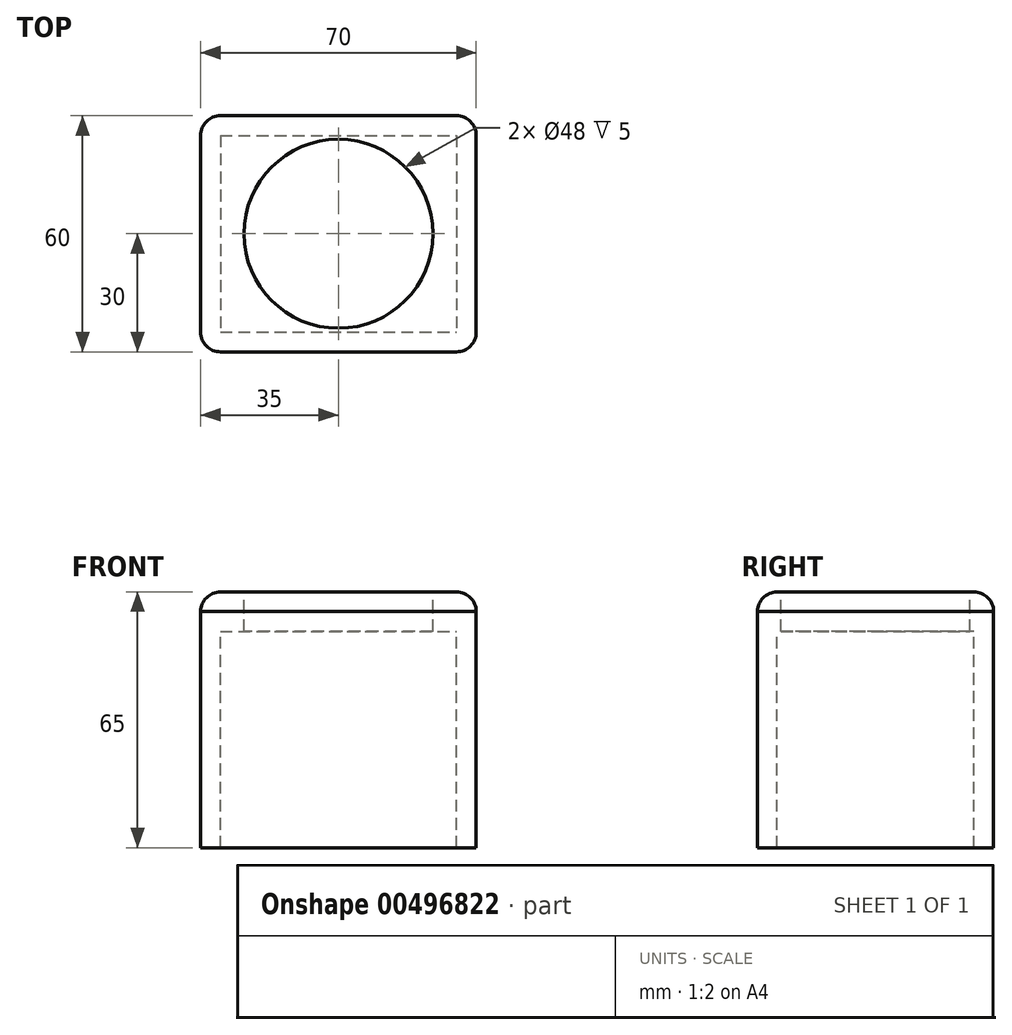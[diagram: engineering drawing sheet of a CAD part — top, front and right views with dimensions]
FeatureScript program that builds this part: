
annotation { "Feature Type Name" : "Feature", "Feature Type Description" : "" }
export const myFeature = defineFeature(function(context is Context, id is Id, definition is map)
    precondition{}
    {
        {
            var Q0;
            Q0=qCreatedBy(makeId("Top.planeOp"),FACE);
            var sketch = newSketch(context, id + "F0", { "sketchPlane" : qUnion([Q0])});
            skLineSegment(sketch, "E0.bottom", {"start": v(0, 0) * mm, "end": v(10, 0) * mm});
            skLineSegment(sketch, "E0.left", {"start": v(0, 0) * mm, "end": v(0, -10) * mm});
            skLineSegment(sketch, "E1.0.1.2", {"start": v(0, -50) * mm, "end": v(0, -60) * mm});
            skLineSegment(sketch, "E1.0.1.3", {"start": v(0, -60) * mm, "end": v(10, -60) * mm});
            skLineSegment(sketch, "E1.1.0.0", {"start": v(70, 0) * mm, "end": v(70, -10) * mm});
            skLineSegment(sketch, "E1.1.0.1", {"start": v(60, 0) * mm, "end": v(70, 0) * mm});
            skLineSegment(sketch, "E1.1.1.0", {"start": v(70, -50) * mm, "end": v(70, -60) * mm});
            skLineSegment(sketch, "E1.1.1.3", {"start": v(60, -60) * mm, "end": v(70, -60) * mm});
            skLineSegment(sketch, "E1.direction1", {"start": v(10, -10) * mm, "end": v(60, -10) * mm});
            skLineSegment(sketch, "E1.direction2", {"start": v(10, -10) * mm, "end": v(10, -50) * mm});
            skLineSegment(sketch, "E2", {"start": v(0, -10) * mm, "end": v(0, -50) * mm});
            skLineSegment(sketch, "E3", {"start": v(10, 0) * mm, "end": v(60, 0) * mm});
            skLineSegment(sketch, "E4", {"start": v(70, -10) * mm, "end": v(70, -50) * mm});
            skLineSegment(sketch, "E5", {"start": v(60, -60) * mm, "end": v(10, -60) * mm});
            skLineSegment(sketch, "E6", {"start": v(10, -50) * mm, "end": v(60, -50) * mm});
            skLineSegment(sketch, "E7", {"start": v(60, -10.5) * mm, "end": v(60, -50.5) * mm});
            skSolve(sketch);
        }
        {
            var Q0;
            Q0 = qSketchRegion(id + "F0", true);
            var Q1;
            Q1 = qSketchRegion(id + "F2", true);
            extrude(context, id + "F1", {"entities" : qUnion([Q0, Q1]), "depth" : 60 * mm, "offsetDistance" : 25 * mm});
        }
        {
            var Q0;
            Q0=qCreatedBy(makeId("Front.planeOp"),FACE);
            var sketch = newSketch(context, id + "F2", { "sketchPlane" : qUnion([Q0])});
            skLineSegment(sketch, "E8.bottom", {"start": v(0, 60) * mm, "end": v(70, 60) * mm});
            skLineSegment(sketch, "E8.top", {"start": v(0, 65) * mm, "end": v(70, 65) * mm});
            skLineSegment(sketch, "E8.left", {"start": v(0, 60) * mm, "end": v(0, 65) * mm});
            skLineSegment(sketch, "E8.right", {"start": v(70, 60) * mm, "end": v(70, 65) * mm});
            skSolve(sketch);
        }
        {
            var Q0;
            Q0=makeQuery(id+"F2.imprint","IMPRINT",FACE,{"disambiguationData":[TD([[makeQuery(id+"F2.imprint","IMPRINT",EDGE,{"derivedFrom":sQuery(id+"F2.wireOp",EDGE,"E8.bottom")}),1.0]])]});
            extrude(context, id + "F3", {"entities" : qUnion([Q0]), "depth" : 60 * mm, "offsetDistance" : 25 * mm});
        }
        {
            var Q0;
            Q0=makeQuery(id+"F3.opExtrude","SWEPT_FACE",FACE,{"disambiguationData":[OSD([sQuery(id+"F2.wireOp",EDGE,"E8.top")])]});
            var sketch = newSketch(context, id + "F4", { "sketchPlane" : qUnion([Q0])});
            skCircle(sketch, "E9", {"center": v(35, -30) * mm, "radius": 25 * mm});
            skSolve(sketch);
        }
        {
            var Q0;
            Q0=sQuery(id+"F4.wireOp",VERTEX,"E9.center");
            var Q1;
            Q1=makeQuery(id+"F3.opExtrude","SWEPT_BODY",BODY,{"disambiguationData":[OSD([sQuery(id+"F2.wireOp",EDGE,"E8.bottom"),sQuery(id+"F2.wireOp",EDGE,"E8.top"),sQuery(id+"F2.wireOp",EDGE,"E8.left"),sQuery(id+"F2.wireOp",EDGE,"E8.right")])]});
            hole(context, id + "F5", {"style" : HoleStyle.SIMPLE, "endStyle" : HoleEndStyle.THROUGH, "holeDiameter" : 48 * mm, "majorDiameter" : 5 * mm, "isTappedThrough" : true, "tappedDepth" : 12 * mm, "tapClearance" : 3, "locations" : qUnion([Q0]), "scope" : qUnion([Q1])});
        }
        {
            var Q0;
            Q0=makeQuery(id+"F3.opExtrude","SWEPT_EDGE",EDGE,{"disambiguationData":[OSD([sQuery(id+"F2.wireOp",EDGE,"E8.top"),sQuery(id+"F2.wireOp",EDGE,"E8.left")])]});
            var Q1;
            Q1=makeQuery(id+"F3.opExtrude","CAP_EDGE",EDGE,{"disambiguationData":[OSD([sQuery(id+"F2.wireOp",EDGE,"E8.top")])],"isStart":true});
            var Q2;
            Q2=makeQuery(id+"F3.opExtrude","SWEPT_EDGE",EDGE,{"disambiguationData":[OSD([sQuery(id+"F2.wireOp",EDGE,"E8.top"),sQuery(id+"F2.wireOp",EDGE,"E8.right")])]});
            var Q3;
            Q3=makeQuery(id+"F3.opExtrude","CAP_EDGE",EDGE,{"disambiguationData":[OSD([sQuery(id+"F2.wireOp",EDGE,"E8.top")])],"isStart":false});
            var Q4;
            Q4=makeQuery(id+"F1.opExtrude","SWEPT_EDGE",EDGE,{"disambiguationData":[OSD([sQuery(id+"F0.wireOp",EDGE,"E1.0.1.2"),sQuery(id+"F0.wireOp",EDGE,"E1.0.1.3")])]});
            var Q5;
            Q5=makeQuery(id+"F1.opExtrude","SWEPT_EDGE",EDGE,{"disambiguationData":[OSD([sQuery(id+"F0.wireOp",EDGE,"E1.1.1.0"),sQuery(id+"F0.wireOp",EDGE,"E1.1.1.3")])]});
            var Q6;
            Q6=makeQuery(id+"F1.opExtrude","SWEPT_EDGE",EDGE,{"disambiguationData":[OSD([sQuery(id+"F0.wireOp",EDGE,"E1.1.0.0"),sQuery(id+"F0.wireOp",EDGE,"E1.1.0.1")])]});
            var Q7;
            Q7=makeQuery(id+"F1.opExtrude","SWEPT_EDGE",EDGE,{"disambiguationData":[OSD([sQuery(id+"F0.wireOp",EDGE,"E0.bottom"),sQuery(id+"F0.wireOp",EDGE,"E0.left")])]});
            var Q8;
            Q8=makeQuery(id+"F3.opExtrude","CAP_EDGE",EDGE,{"disambiguationData":[OSD([sQuery(id+"F2.wireOp",EDGE,"E8.left")])],"isStart":true});
            var Q9;
            Q9=makeQuery(id+"F3.opExtrude","CAP_EDGE",EDGE,{"disambiguationData":[OSD([sQuery(id+"F2.wireOp",EDGE,"E8.left")])],"isStart":false});
            var Q10;
            Q10=makeQuery(id+"F3.opExtrude","CAP_EDGE",EDGE,{"disambiguationData":[OSD([sQuery(id+"F2.wireOp",EDGE,"E8.right")])],"isStart":true});
            var Q11;
            Q11=makeQuery(id+"F3.opExtrude","CAP_EDGE",EDGE,{"disambiguationData":[OSD([sQuery(id+"F2.wireOp",EDGE,"E8.right")])],"isStart":false});
            fillet(context, id + "F6", {"entities" : qUnion([Q0, Q1, Q2, Q3, Q4, Q5, Q6, Q7, Q8, Q9, Q10, Q11]), "radius" : 5 * mm, "tangentPropagation" : true, "allowEdgeOverflow" : false});
        }
        {
            var Q0;
            Q0=makeQuery(id+"F1.opExtrude","CAP_FACE",FACE,{"disambiguationData":[OSD([sQuery(id+"F0.wireOp",EDGE,"E0.bottom"),sQuery(id+"F0.wireOp",EDGE,"E0.left"),sQuery(id+"F0.wireOp",EDGE,"E1.0.1.2"),sQuery(id+"F0.wireOp",EDGE,"E1.0.1.3"),sQuery(id+"F0.wireOp",EDGE,"E1.1.0.0"),sQuery(id+"F0.wireOp",EDGE,"E1.1.0.1"),sQuery(id+"F0.wireOp",EDGE,"E1.1.1.0"),sQuery(id+"F0.wireOp",EDGE,"E1.1.1.3"),sQuery(id+"F0.wireOp",EDGE,"E2"),sQuery(id+"F0.wireOp",EDGE,"E3"),sQuery(id+"F0.wireOp",EDGE,"E4"),sQuery(id+"F0.wireOp",EDGE,"E5")])],"isStart":true});
            shell(context, id + "F7", {"entities" : qUnion([Q0]), "thickness" : 5 * mm});
        }
        {
            var Q0;
            Q0=sQuery(id+"F4.wireOp",VERTEX,"E9.center");
            var Q1;
            Q1=makeQuery(id+"F1.opExtrude","SWEPT_BODY",BODY,{"disambiguationData":[OSD([sQuery(id+"F0.wireOp",EDGE,"E0.bottom"),sQuery(id+"F0.wireOp",EDGE,"E0.left"),sQuery(id+"F0.wireOp",EDGE,"E1.0.1.2"),sQuery(id+"F0.wireOp",EDGE,"E1.0.1.3"),sQuery(id+"F0.wireOp",EDGE,"E1.1.0.0"),sQuery(id+"F0.wireOp",EDGE,"E1.1.0.1"),sQuery(id+"F0.wireOp",EDGE,"E1.1.1.0"),sQuery(id+"F0.wireOp",EDGE,"E1.1.1.3"),sQuery(id+"F0.wireOp",EDGE,"E2"),sQuery(id+"F0.wireOp",EDGE,"E3"),sQuery(id+"F0.wireOp",EDGE,"E4"),sQuery(id+"F0.wireOp",EDGE,"E5")])]});
            hole(context, id + "F8", {"style" : HoleStyle.SIMPLE, "endStyle" : HoleEndStyle.THROUGH, "holeDiameter" : 48 * mm, "majorDiameter" : 5 * mm, "isTappedThrough" : true, "tappedDepth" : 12 * mm, "tapClearance" : 3, "locations" : qUnion([Q0]), "scope" : qUnion([Q1])});
        }
    });
